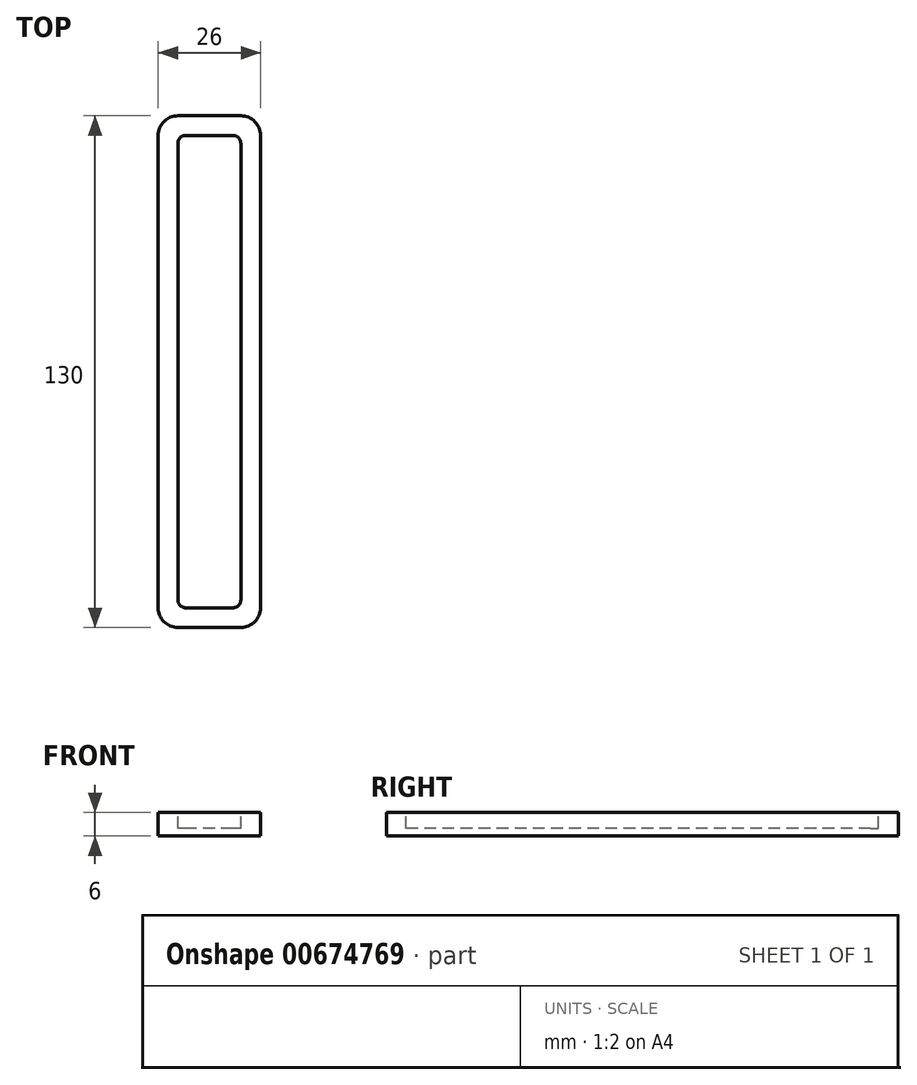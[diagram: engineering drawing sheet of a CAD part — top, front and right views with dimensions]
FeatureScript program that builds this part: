
annotation { "Feature Type Name" : "Feature", "Feature Type Description" : "" }
export const myFeature = defineFeature(function(context is Context, id is Id, definition is map)
    precondition{}
    {
        {
            var Q0;
            Q0=qCreatedBy(makeId("Top.planeOp"),FACE);
            var sketch = newSketch(context, id + "F0", { "sketchPlane" : qUnion([Q0])});
            skLineSegment(sketch, "E0.bottom", {"start": v(13, 65) * mm, "end": v(-13, 65) * mm});
            skLineSegment(sketch, "E0.top", {"start": v(13, -65) * mm, "end": v(-13, -65) * mm});
            skLineSegment(sketch, "E0.left", {"start": v(13, 65) * mm, "end": v(13, -65) * mm});
            skLineSegment(sketch, "E0.right", {"start": v(-13, 65) * mm, "end": v(-13, -65) * mm});
            skPoint(sketch, "E0.middle", {"position": v(0, 0) * mm});
            skSolve(sketch);
        }
        {
            var Q0;
            Q0 = qSketchRegion(id + "F0", true);
            extrude(context, id + "F1", {"entities" : qUnion([Q0]), "depth" : 6 * mm, "offsetDistance" : 25 * mm});
        }
        {
            var Q0;
            Q0=makeQuery(id+"F1.opExtrude","CAP_FACE",FACE,{"disambiguationData":[OSD([sQuery(id+"F0.wireOp",EDGE,"E0.bottom"),sQuery(id+"F0.wireOp",EDGE,"E0.top"),sQuery(id+"F0.wireOp",EDGE,"E0.left"),sQuery(id+"F0.wireOp",EDGE,"E0.right")])],"isStart":false});
            var sketch = newSketch(context, id + "F2", { "sketchPlane" : qUnion([Q0])});
            skLineSegment(sketch, "E1.bottom", {"start": v(8, 60) * mm, "end": v(-8, 60) * mm});
            skLineSegment(sketch, "E1.top", {"start": v(8, -60) * mm, "end": v(-8, -60) * mm});
            skLineSegment(sketch, "E1.left", {"start": v(8, 60) * mm, "end": v(8, -60) * mm});
            skLineSegment(sketch, "E1.right", {"start": v(-8, 60) * mm, "end": v(-8, -60) * mm});
            skPoint(sketch, "E1.middle", {"position": v(0, 0) * mm});
            skSolve(sketch);
        }
        {
            var Q0;
            Q0 = qSketchRegion(id + "F2", true);
            extrude(context, id + "F3", {"entities" : qUnion([Q0]), "operationType" : NewBodyOperationType.REMOVE, "oppositeDirection" : true, "depth" : 4 * mm, "offsetDistance" : 25 * mm});
        }
        {
            var Q0;
            Q0=makeQuery(id+"F3.boolean.opBoolean","COPY",EDGE,{"derivedFrom":makeQuery(id+"F3.opExtrude","SWEPT_EDGE",EDGE,{"disambiguationData":[OSD([sQuery(id+"F2.wireOp",EDGE,"E1.bottom"),sQuery(id+"F2.wireOp",EDGE,"E1.right")])]})});
            var Q1;
            Q1=makeQuery(id+"F3.boolean.opBoolean","COPY",EDGE,{"derivedFrom":makeQuery(id+"F3.opExtrude","SWEPT_EDGE",EDGE,{"disambiguationData":[OSD([sQuery(id+"F2.wireOp",EDGE,"E1.top"),sQuery(id+"F2.wireOp",EDGE,"E1.right")])]})});
            var Q2;
            Q2=makeQuery(id+"F3.boolean.opBoolean","COPY",EDGE,{"derivedFrom":makeQuery(id+"F3.opExtrude","SWEPT_EDGE",EDGE,{"disambiguationData":[OSD([sQuery(id+"F2.wireOp",EDGE,"E1.top"),sQuery(id+"F2.wireOp",EDGE,"E1.left")])]})});
            var Q3;
            Q3=makeQuery(id+"F3.boolean.opBoolean","COPY",EDGE,{"derivedFrom":makeQuery(id+"F3.opExtrude","SWEPT_EDGE",EDGE,{"disambiguationData":[OSD([sQuery(id+"F2.wireOp",EDGE,"E1.bottom"),sQuery(id+"F2.wireOp",EDGE,"E1.left")])]})});
            fillet(context, id + "F4", {"entities" : qUnion([Q0, Q1, Q2, Q3]), "radius" : 2 * mm, "tangentPropagation" : true, "allowEdgeOverflow" : false});
        }
        {
            var Q0;
            Q0=makeQuery(id+"F1.opExtrude","SWEPT_EDGE",EDGE,{"disambiguationData":[OSD([sQuery(id+"F0.wireOp",EDGE,"E0.top"),sQuery(id+"F0.wireOp",EDGE,"E0.right")])]});
            var Q1;
            Q1=makeQuery(id+"F1.opExtrude","SWEPT_EDGE",EDGE,{"disambiguationData":[OSD([sQuery(id+"F0.wireOp",EDGE,"E0.top"),sQuery(id+"F0.wireOp",EDGE,"E0.left")])]});
            var Q2;
            Q2=makeQuery(id+"F1.opExtrude","SWEPT_EDGE",EDGE,{"disambiguationData":[OSD([sQuery(id+"F0.wireOp",EDGE,"E0.bottom"),sQuery(id+"F0.wireOp",EDGE,"E0.left")])]});
            var Q3;
            Q3=makeQuery(id+"F1.opExtrude","SWEPT_EDGE",EDGE,{"disambiguationData":[OSD([sQuery(id+"F0.wireOp",EDGE,"E0.bottom"),sQuery(id+"F0.wireOp",EDGE,"E0.right")])]});
            fillet(context, id + "F5", {"entities" : qUnion([Q0, Q1, Q2, Q3]), "radius" : 5 * mm, "tangentPropagation" : true, "allowEdgeOverflow" : false});
        }
    });
